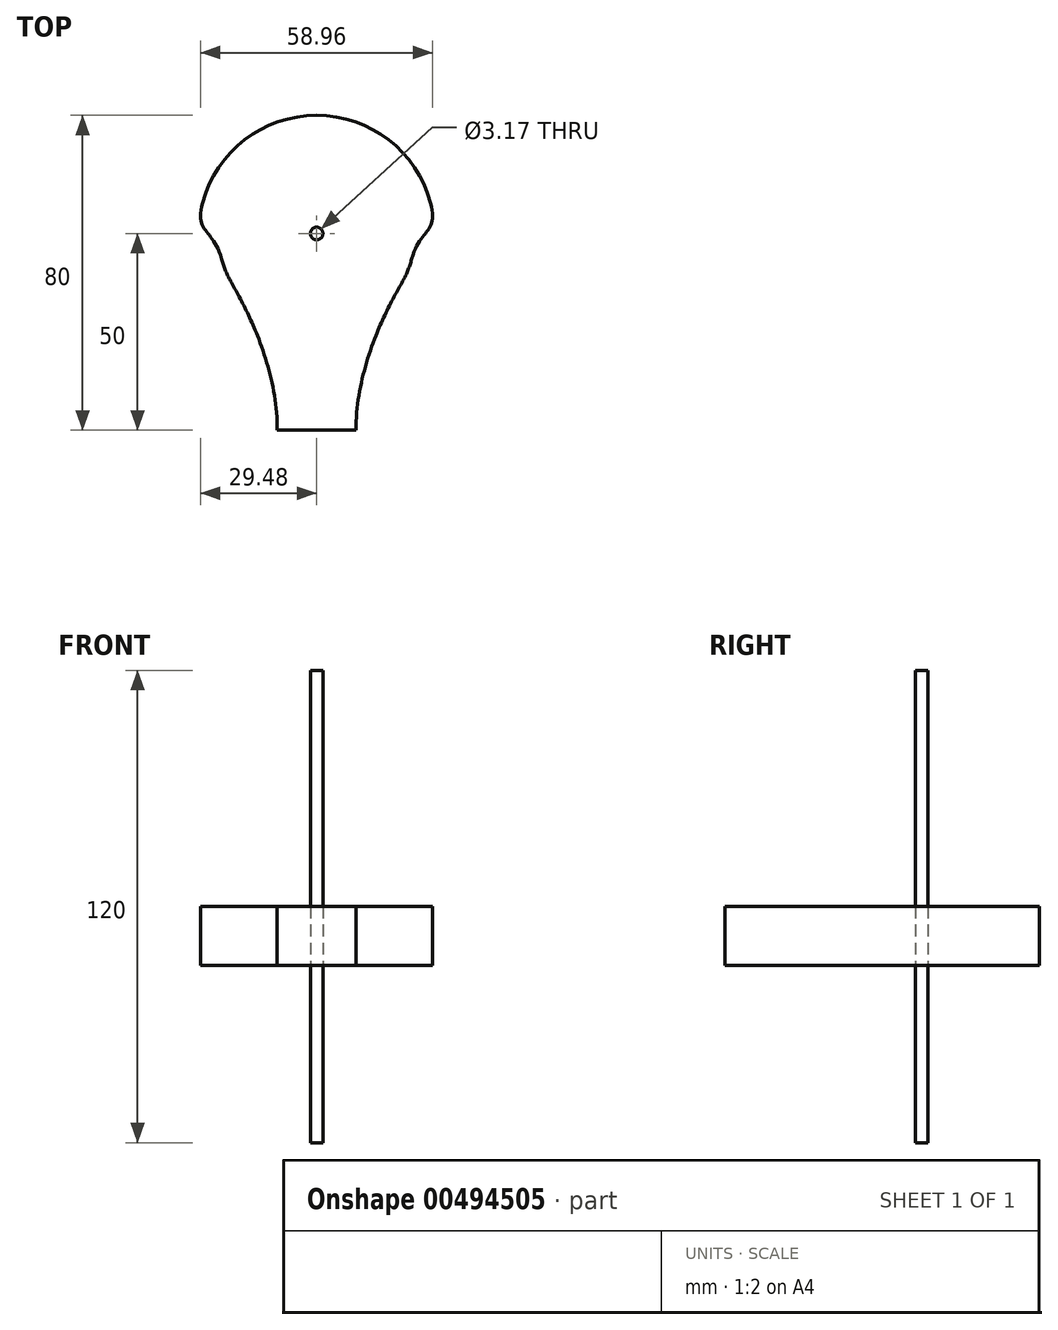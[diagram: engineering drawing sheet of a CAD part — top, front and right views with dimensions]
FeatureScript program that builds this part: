
annotation { "Feature Type Name" : "Feature", "Feature Type Description" : "" }
export const myFeature = defineFeature(function(context is Context, id is Id, definition is map)
    precondition{}
    {
        {
            var Q0;
            Q0=qCreatedBy(makeId("Top.planeOp"),FACE);
            var sketch = newSketch(context, id + "F0", { "sketchPlane" : qUnion([Q0])});
            skLineSegment(sketch, "E0.bottom", {"start": v(10, 25) * mm, "end": v(-10, 25) * mm, "construction": true});
            skLineSegment(sketch, "E0.top", {"start": v(10, -25) * mm, "end": v(-10, -25) * mm});
            skLineSegment(sketch, "E0.left", {"start": v(10, 25) * mm, "end": v(10, -25) * mm, "construction": true});
            skLineSegment(sketch, "E0.right", {"start": v(-10, 25) * mm, "end": v(-10, -25) * mm, "construction": true});
            skPoint(sketch, "E0.middle", {"position": v(0, 0) * mm});
            skCircle(sketch, "E1", {"center": v(0, 25) * mm, "radius": 25 * mm});
            skCircle(sketch, "E2", {"center": v(0, 25) * mm, "radius": 30 * mm});
            skLineSegment(sketch, "E3", {"start": v(0, 25) * mm, "end": v(28.98, 32.76) * mm});
            skLineSegment(sketch, "E4", {"start": v(0, 25) * mm, "end": v(24.15, 18.53) * mm});
            skLineSegment(sketch, "E5", {"start": v(0, 25) * mm, "end": v(21.65, 12.5) * mm});
            skLineSegment(sketch, "E6", {"start": v(0, 25) * mm, "end": v(25.98, 40) * mm});
            skFitSpline(sketch, "E7", {"points": [v(24.15, 18.53) * mm, v(28.98, 32.76) * mm], "startDerivative": vector(6.21, 23.18) * mm, "endDerivative": vector(-6.21, 23.18) * mm});
            skLineSegment(sketch, "E8", {"start": v(28.98, 32.76) * mm, "end": v(31.05, 25.04) * mm});
            skLineSegment(sketch, "E9", {"start": v(24.15, 18.53) * mm, "end": v(26.22, 26.26) * mm});
            skFitSpline(sketch, "E10", {"points": [v(21.65, 12.5) * mm, v(10, -25) * mm], "startDerivative": vector(-15, -25.98) * mm, "endDerivative": vector(0, -45) * mm});
            skLineSegment(sketch, "E11", {"start": v(21.65, 12.5) * mm, "end": v(16.65, 3.84) * mm});
            skLineSegment(sketch, "E12", {"start": v(0, -25) * mm, "end": v(0, 55) * mm, "construction": true});
            skFitSpline(sketch, "E13.MirrorCS", {"points": [v(-24.15, 18.53) * mm, v(-28.98, 32.76) * mm], "startDerivative": vector(-6.21, 23.18) * mm, "endDerivative": vector(6.21, 23.18) * mm});
            skFitSpline(sketch, "E14.MirrorCS", {"points": [v(-21.65, 12.5) * mm, v(-10, -25) * mm], "startDerivative": vector(15, -25.98) * mm, "endDerivative": vector(0, -45) * mm});
            skLineSegment(sketch, "E15.MirrorCS", {"start": v(0, 25) * mm, "end": v(-25.98, 40) * mm});
            skSolve(sketch);
        }
        {
            var Q0;
            {var subQ0=sQuery(id+"F0.wireOp",EDGE,"E6");var subQ1=sQuery(id+"F0.wireOp",EDGE,"E1");var subQ2=makeQuery(id+"F0.imprint","INTERSECT",VERTEX,{"derivedFrom":[subQ1,subQ0]});Q0=makeQuery(id+"F0.imprint","IMPRINT",FACE,{"disambiguationData":[TD([[makeQuery(id+"F0.imprint","IMPRINT",EDGE,{"disambiguationData":[TD([[subQ2,-1.0]])],"derivedFrom":subQ1}),1.0]])]});}
            var Q1;
            {var subQ0=sQuery(id+"F0.wireOp",EDGE,"E6");var subQ1=sQuery(id+"F0.wireOp",EDGE,"E1");var subQ2=makeQuery(id+"F0.imprint","INTERSECT",VERTEX,{"derivedFrom":[subQ1,subQ0]});Q1=makeQuery(id+"F0.imprint","IMPRINT",FACE,{"disambiguationData":[TD([[makeQuery(id+"F0.imprint","IMPRINT",EDGE,{"disambiguationData":[TD([[subQ2,-1.0]])],"derivedFrom":subQ1}),-1.0]])]});}
            var Q2;
            {var subQ0=sQuery(id+"F0.wireOp",EDGE,"E6");var subQ1=sQuery(id+"F0.wireOp",EDGE,"E1");var subQ2=makeQuery(id+"F0.imprint","INTERSECT",VERTEX,{"derivedFrom":[subQ1,subQ0]});Q2=makeQuery(id+"F0.imprint","IMPRINT",FACE,{"disambiguationData":[TD([[makeQuery(id+"F0.imprint","IMPRINT",EDGE,{"disambiguationData":[TD([[subQ2,1.0]])],"derivedFrom":subQ1}),1.0]])]});}
            var Q3;
            {var subQ0=sQuery(id+"F0.wireOp",EDGE,"E6");var subQ1=sQuery(id+"F0.wireOp",EDGE,"E1");var subQ2=makeQuery(id+"F0.imprint","INTERSECT",VERTEX,{"derivedFrom":[subQ1,subQ0]});Q3=makeQuery(id+"F0.imprint","IMPRINT",FACE,{"disambiguationData":[TD([[makeQuery(id+"F0.imprint","IMPRINT",EDGE,{"disambiguationData":[TD([[subQ2,1.0]])],"derivedFrom":subQ1}),-1.0]])]});}
            var Q4;
            {var subQ0=sQuery(id+"F0.wireOp",EDGE,"E4");Q4=makeQuery(id+"F0.imprint","IMPRINT",FACE,{"disambiguationData":[TD([[makeQuery(id+"F0.imprint","IMPRINT",EDGE,{"derivedFrom":subQ0}),1.0]])]});}
            var Q5;
            {var subQ0=sQuery(id+"F0.wireOp",EDGE,"E7");Q5=makeQuery(id+"F0.imprint","IMPRINT",FACE,{"disambiguationData":[TD([[makeQuery(id+"F0.imprint","IMPRINT",EDGE,{"derivedFrom":subQ0}),1.0]])]});}
            var Q6;
            {var subQ0=sQuery(id+"F0.wireOp",EDGE,"E4");Q6=makeQuery(id+"F0.imprint","IMPRINT",FACE,{"disambiguationData":[TD([[makeQuery(id+"F0.imprint","IMPRINT",EDGE,{"derivedFrom":subQ0}),-1.0]])]});}
            var Q7;
            {var subQ0=sQuery(id+"F0.wireOp",EDGE,"E5");Q7=makeQuery(id+"F0.imprint","IMPRINT",FACE,{"disambiguationData":[TD([[makeQuery(id+"F0.imprint","IMPRINT",EDGE,{"derivedFrom":subQ0}),-1.0]])]});}
            var Q8;
            {var subQ3=sQuery(id+"F0.wireOp",EDGE,"E14.MirrorCS");var subQ5=sQuery(id+"F0.wireOp",EDGE,"E2");var subQ6=makeQuery(id+"F0.imprint","INTERSECT",VERTEX,{"derivedFrom":[subQ5,subQ3]});Q8=makeQuery(id+"F0.imprint","IMPRINT",FACE,{"disambiguationData":[TD([[makeQuery(id+"F0.imprint","IMPRINT",EDGE,{"disambiguationData":[TD([[subQ6,-1.0]])],"derivedFrom":subQ5}),1.0]])]});}
            var Q9;
            {var subQ0=sQuery(id+"F0.wireOp",EDGE,"E0.top");Q9=makeQuery(id+"F0.imprint","IMPRINT",FACE,{"disambiguationData":[TD([[makeQuery(id+"F0.imprint","IMPRINT",EDGE,{"derivedFrom":subQ0}),-1.0]])]});}
            var Q10;
            {var subQ0=sQuery(id+"F0.wireOp",EDGE,"E13.MirrorCS");Q10=makeQuery(id+"F0.imprint","IMPRINT",FACE,{"disambiguationData":[TD([[makeQuery(id+"F0.imprint","IMPRINT",EDGE,{"derivedFrom":subQ0}),-1.0]])]});}
            extrude(context, id + "F1", {"entities" : qUnion([Q0, Q1, Q2, Q3, Q4, Q5, Q6, Q7, Q8, Q9, Q10]), "depth" : 15 * mm, "offsetDistance" : 25.4 * mm});
        }
        {
            var Q0;
            Q0=makeQuery(id+"F1.opExtrude","CAP_FACE",FACE,{"disambiguationData":[OSD([sQuery(id+"F0.wireOp",EDGE,"E0.top"),sQuery(id+"F0.wireOp",EDGE,"E1"),sQuery(id+"F0.wireOp",EDGE,"E2"),sQuery(id+"F0.wireOp",EDGE,"E7"),sQuery(id+"F0.wireOp",EDGE,"E10"),sQuery(id+"F0.wireOp",EDGE,"E13.MirrorCS"),sQuery(id+"F0.wireOp",EDGE,"E14.MirrorCS")])],"isStart":false});
            var sketch = newSketch(context, id + "F2", { "sketchPlane" : qUnion([Q0])});
            skCircle(sketch, "E16", {"center": v(0, 25) * mm, "radius": 1.59 * mm});
            skSolve(sketch);
        }
        {
            var Q0;
            Q0 = qSketchRegion(id + "F2", true);
            extrude(context, id + "F3", {"entities" : qUnion([Q0]), "operationType" : NewBodyOperationType.REMOVE, "oppositeDirection" : true, "depth" : 25 * mm, "offsetDistance" : 25 * mm});
        }
        {
            var Q0;
            Q0=makeQuery(id+"F1.opExtrude","CAP_FACE",FACE,{"disambiguationData":[OSD([sQuery(id+"F0.wireOp",EDGE,"E0.top"),sQuery(id+"F0.wireOp",EDGE,"E1"),sQuery(id+"F0.wireOp",EDGE,"E2"),sQuery(id+"F0.wireOp",EDGE,"E7"),sQuery(id+"F0.wireOp",EDGE,"E10"),sQuery(id+"F0.wireOp",EDGE,"E13.MirrorCS"),sQuery(id+"F0.wireOp",EDGE,"E14.MirrorCS")])],"isStart":false});
            var sketch = newSketch(context, id + "F4", { "sketchPlane" : qUnion([Q0])});
            skCircle(sketch, "E17", {"center": v(0, 25) * mm, "radius": 1.59 * mm});
            skSolve(sketch);
        }
        {
            var Q0;
            Q0 = qSketchRegion(id + "F4", true);
            extrude(context, id + "F5", {"entities" : qUnion([Q0]), "depth" : 60 * mm, "offsetDistance" : 25 * mm, "hasSecondDirection" : true, "secondDirectionOppositeDirection" : true, "secondDirectionDepth" : 60 * mm});
        }
    });
